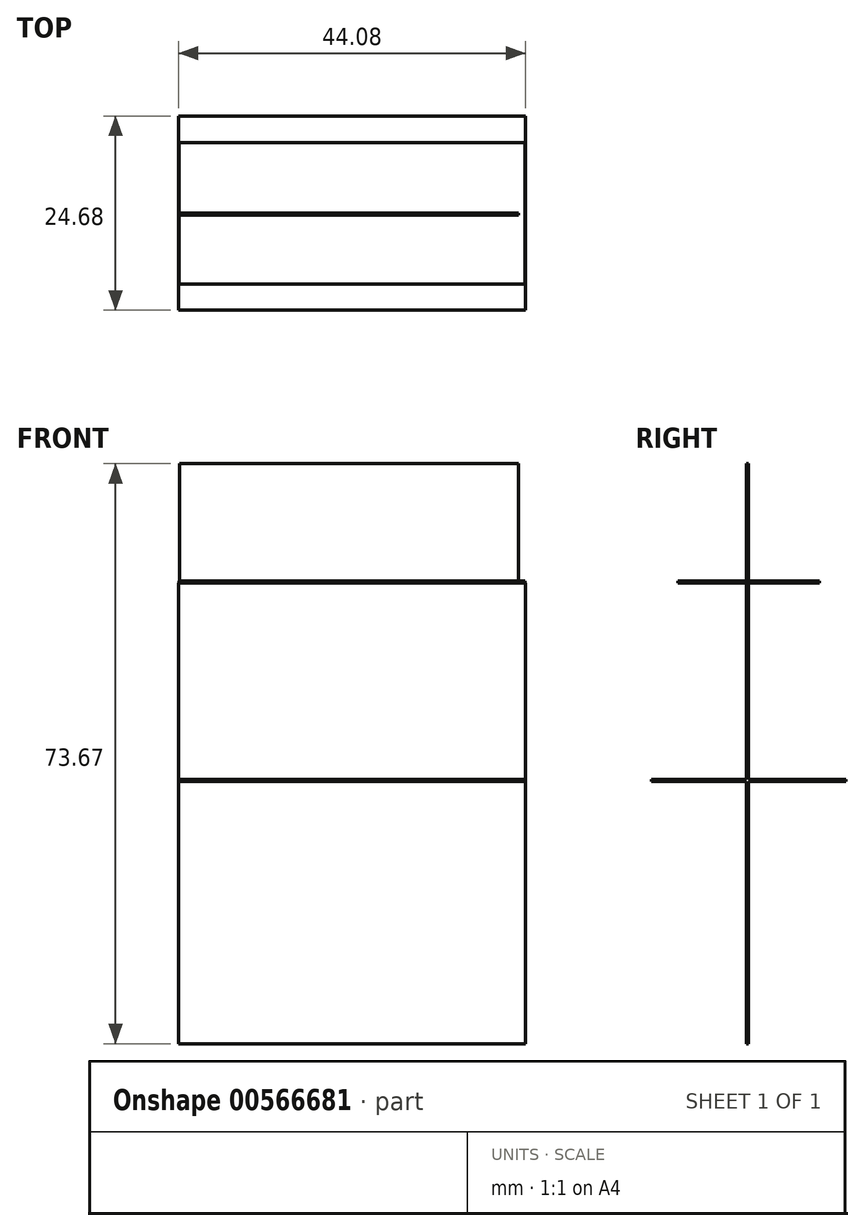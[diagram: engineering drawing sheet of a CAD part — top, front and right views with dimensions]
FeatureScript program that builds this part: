
annotation { "Feature Type Name" : "Feature", "Feature Type Description" : "" }
export const myFeature = defineFeature(function(context is Context, id is Id, definition is map)
    precondition{}
    {
        {
            var Q0;
            Q0=qCreatedBy(makeId("Front.planeOp"),FACE);
            var sketch = newSketch(context, id + "F0", { "sketchPlane" : qUnion([Q0])});
            skLineSegment(sketch, "E0.bottom", {"start": v(22.04, -33.32) * mm, "end": v(-22.04, -33.32) * mm});
            skLineSegment(sketch, "E0.top", {"start": v(22.04, 0) * mm, "end": v(-22.04, 0) * mm});
            skLineSegment(sketch, "E0.left", {"start": v(22.04, -33.32) * mm, "end": v(22.04, 0) * mm});
            skLineSegment(sketch, "E0.right", {"start": v(-22.04, -33.32) * mm, "end": v(-22.04, 0) * mm});
            skPoint(sketch, "E0.middle", {"position": v(0, -16.66) * mm});
            skSolve(sketch);
        }
        {
            var Q0;
            Q0 = qSketchRegion(id + "F0", true);
            extrude(context, id + "F1", {"entities" : qUnion([Q0]), "depth" : 0.25 * mm, "offsetDistance" : 25.4 * mm});
        }
        {
            var Q0;
            Q0=makeQuery(id+"F1.opExtrude","SWEPT_FACE",FACE,{"disambiguationData":[OSD([sQuery(id+"F0.wireOp",EDGE,"E0.top")])]});
            var sketch = newSketch(context, id + "F2", { "sketchPlane" : qUnion([Q0])});
            skLineSegment(sketch, "E1.bottom", {"start": v(22.04, -12.34) * mm, "end": v(-22.04, -12.34) * mm});
            skLineSegment(sketch, "E1.top", {"start": v(22.04, 12.34) * mm, "end": v(-22.04, 12.34) * mm});
            skLineSegment(sketch, "E1.left", {"start": v(22.04, -12.34) * mm, "end": v(22.04, 12.34) * mm});
            skLineSegment(sketch, "E1.right", {"start": v(-22.04, -12.34) * mm, "end": v(-22.04, 12.34) * mm});
            skPoint(sketch, "E1.middle", {"position": v(0, 0) * mm});
            skSolve(sketch);
        }
        {
            var Q0;
            Q0 = qSketchRegion(id + "F2", true);
            extrude(context, id + "F3", {"entities" : qUnion([Q0]), "operationType" : NewBodyOperationType.ADD, "depth" : 0.25 * mm, "offsetDistance" : 25.4 * mm});
        }
        {
            var Q0;
            Q0=qCreatedBy(makeId("Front.planeOp"),FACE);
            var sketch = newSketch(context, id + "F4", { "sketchPlane" : qUnion([Q0])});
            skLineSegment(sketch, "E2.bottom", {"start": v(-22.04, 0) * mm, "end": v(22.04, 0) * mm});
            skLineSegment(sketch, "E2.top", {"start": v(-22.04, 25.17) * mm, "end": v(22.04, 25.17) * mm});
            skLineSegment(sketch, "E2.left", {"start": v(-22.04, 0) * mm, "end": v(-22.04, 25.17) * mm});
            skLineSegment(sketch, "E2.right", {"start": v(22.04, 0) * mm, "end": v(22.04, 25.17) * mm});
            skSolve(sketch);
        }
        {
            var Q0;
            Q0 = qSketchRegion(id + "F4", true);
            extrude(context, id + "F5", {"entities" : qUnion([Q0]), "operationType" : NewBodyOperationType.ADD, "depth" : 0.25 * mm, "offsetDistance" : 25.4 * mm});
        }
        {
            var Q0;
            Q0=makeQuery(id+"F5.opExtrude","SWEPT_FACE",FACE,{"disambiguationData":[OSD([sQuery(id+"F4.wireOp",EDGE,"E2.top")])]});
            var sketch = newSketch(context, id + "F6", { "sketchPlane" : qUnion([Q0])});
            skLineSegment(sketch, "E3.bottom", {"start": v(22, -8.98) * mm, "end": v(-22, -8.98) * mm});
            skLineSegment(sketch, "E3.top", {"start": v(22, 8.98) * mm, "end": v(-22, 8.98) * mm});
            skLineSegment(sketch, "E3.left", {"start": v(22, -8.98) * mm, "end": v(22, 8.98) * mm});
            skLineSegment(sketch, "E3.right", {"start": v(-22, -8.98) * mm, "end": v(-22, 8.98) * mm});
            skPoint(sketch, "E3.middle", {"position": v(0, 0) * mm});
            skSolve(sketch);
        }
        {
            var Q0;
            Q0 = qSketchRegion(id + "F6", true);
            extrude(context, id + "F7", {"entities" : qUnion([Q0]), "operationType" : NewBodyOperationType.ADD, "depth" : 0.25 * mm, "offsetDistance" : 25.4 * mm});
        }
        {
            var Q0;
            Q0=qCreatedBy(makeId("Front.planeOp"),FACE);
            var sketch = newSketch(context, id + "F8", { "sketchPlane" : qUnion([Q0])});
            skLineSegment(sketch, "E4.bottom", {"start": v(21.15, 24.53) * mm, "end": v(-21.87, 24.53) * mm});
            skLineSegment(sketch, "E4.top", {"start": v(21.15, 40.35) * mm, "end": v(-21.87, 40.35) * mm});
            skLineSegment(sketch, "E4.left", {"start": v(21.15, 24.53) * mm, "end": v(21.15, 40.35) * mm});
            skLineSegment(sketch, "E4.right", {"start": v(-21.87, 24.53) * mm, "end": v(-21.87, 40.35) * mm});
            skSolve(sketch);
        }
        {
            var Q0;
            Q0=makeQuery(id+"F8.imprint","IMPRINT",FACE,{"disambiguationData":[TD([[makeQuery(id+"F8.imprint","IMPRINT",EDGE,{"derivedFrom":sQuery(id+"F8.wireOp",EDGE,"E4.bottom")}),-1.0]])]});
            extrude(context, id + "F9", {"entities" : qUnion([Q0]), "operationType" : NewBodyOperationType.ADD, "depth" : 0.25 * mm, "offsetDistance" : 25.4 * mm});
        }
    });
